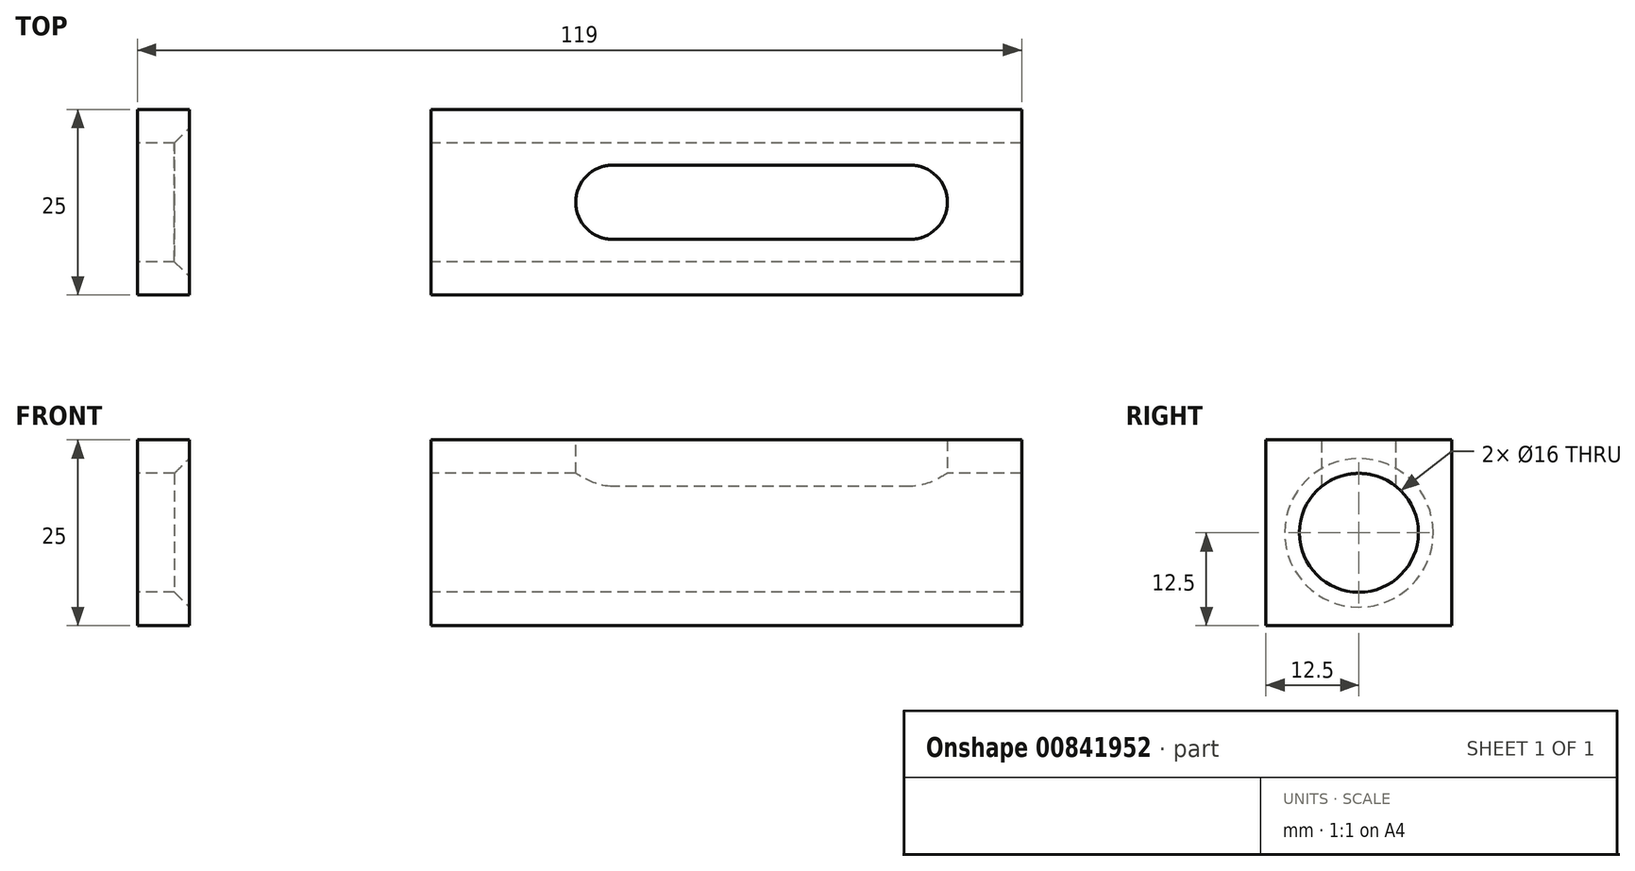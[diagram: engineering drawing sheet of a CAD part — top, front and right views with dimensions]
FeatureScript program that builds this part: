
annotation { "Feature Type Name" : "Feature", "Feature Type Description" : "" }
export const myFeature = defineFeature(function(context is Context, id is Id, definition is map)
    precondition{}
    {
        {
            var Q0;
            Q0=qCreatedBy(makeId("Top.planeOp"),FACE);
            var sketch = newSketch(context, id + "F0", { "sketchPlane" : qUnion([Q0])});
            skLineSegment(sketch, "E0.bottom", {"start": v(-59.5, 12.5) * mm, "end": v(59.5, 12.5) * mm});
            skLineSegment(sketch, "E0.top", {"start": v(-59.5, -12.5) * mm, "end": v(59.5, -12.5) * mm});
            skLineSegment(sketch, "E0.left", {"start": v(-59.5, 12.5) * mm, "end": v(-59.5, -12.5) * mm});
            skLineSegment(sketch, "E0.right", {"start": v(59.5, 12.5) * mm, "end": v(59.5, -12.5) * mm});
            skPoint(sketch, "E0.middle", {"position": v(0, 0) * mm});
            skSolve(sketch);
        }
        {
            var Q0;
            Q0 = qSketchRegion(id + "F0", true);
            extrude(context, id + "F1", {"entities" : qUnion([Q0]), "depth" : 25 * mm, "offsetDistance" : 25 * mm});
        }
        {
            var Q0;
            Q0=makeQuery(id+"F1.opExtrude","SWEPT_FACE",FACE,{"disambiguationData":[OSD([sQuery(id+"F0.wireOp",EDGE,"E0.left")])]});
            var sketch = newSketch(context, id + "F2", { "sketchPlane" : qUnion([Q0])});
            skLineSegment(sketch, "E1", {"start": v(0, 25) * mm, "end": v(0, 0) * mm});
            skCircle(sketch, "E2", {"center": v(0, 12.5) * mm, "radius": 8 * mm});
            skSolve(sketch);
        }
        {
            var Q0;
            {var subQ0=sQuery(id+"F2.wireOp",EDGE,"E2");var subQ1=sQuery(id+"F2.wireOp",EDGE,"E1");var subQ2=makeQuery(id+"F2.imprint","INTERSECT",VERTEX,{"disambiguationData":[OD(0.0)],"derivedFrom":[subQ1,subQ0]});Q0=makeQuery(id+"F2.imprint","IMPRINT",FACE,{"disambiguationData":[TD([[makeQuery(id+"F2.imprint","IMPRINT",EDGE,{"disambiguationData":[TD([[subQ2,-1.0]])],"derivedFrom":subQ1}),1.0]])]});}
            var Q1;
            {var subQ0=sQuery(id+"F2.wireOp",EDGE,"E2");var subQ1=sQuery(id+"F2.wireOp",EDGE,"E1");var subQ2=makeQuery(id+"F2.imprint","INTERSECT",VERTEX,{"disambiguationData":[OD(0.0)],"derivedFrom":[subQ1,subQ0]});Q1=makeQuery(id+"F2.imprint","IMPRINT",FACE,{"disambiguationData":[TD([[makeQuery(id+"F2.imprint","IMPRINT",EDGE,{"disambiguationData":[TD([[subQ2,-1.0]])],"derivedFrom":subQ1}),-1.0]])]});}
            extrude(context, id + "F3", {"entities" : qUnion([Q0, Q1]), "operationType" : NewBodyOperationType.REMOVE, "endBound" : BoundingType.THROUGH_ALL, "oppositeDirection" : true, "depth" : 25 * mm, "offsetDistance" : 25 * mm});
        }
        {
            var Q0;
            Q0=makeQuery(id+"F1.opExtrude","CAP_FACE",FACE,{"disambiguationData":[OSD([sQuery(id+"F0.wireOp",EDGE,"E0.bottom"),sQuery(id+"F0.wireOp",EDGE,"E0.top"),sQuery(id+"F0.wireOp",EDGE,"E0.left"),sQuery(id+"F0.wireOp",EDGE,"E0.right")])],"isStart":false});
            var sketch = newSketch(context, id + "F4", { "sketchPlane" : qUnion([Q0])});
            skLineSegment(sketch, "E3.bottom", {"start": v(-52.5, 12.5) * mm, "end": v(-20, 12.5) * mm});
            skLineSegment(sketch, "E3.top", {"start": v(-52.5, -12.5) * mm, "end": v(-20, -12.5) * mm});
            skLineSegment(sketch, "E3.left", {"start": v(-52.5, 12.5) * mm, "end": v(-52.5, -12.5) * mm});
            skLineSegment(sketch, "E3.right", {"start": v(-20, 12.5) * mm, "end": v(-20, -12.5) * mm});
            skSolve(sketch);
        }
        {
            var Q0;
            Q0 = qSketchRegion(id + "F4", true);
            extrude(context, id + "F5", {"entities" : qUnion([Q0]), "operationType" : NewBodyOperationType.REMOVE, "endBound" : BoundingType.THROUGH_ALL, "oppositeDirection" : true, "depth" : 25 * mm, "offsetDistance" : 25 * mm});
        }
        {
            var Q0;
            Q0=makeQuery(id+"F5.boolean.opBoolean","INTERSECT",EDGE,{"derivedFrom":[makeQuery(id+"F3.boolean.opBoolean","COPY",FACE,{"derivedFrom":makeQuery(id+"F3.opExtrude","SWEPT_FACE",FACE,{"disambiguationData":[OSD([sQuery(id+"F2.wireOp",EDGE,"E2")])]})}),makeQuery(id+"F5.opExtrude","SWEPT_FACE",FACE,{"disambiguationData":[OSD([sQuery(id+"F4.wireOp",EDGE,"E3.left")])]})]});
            chamfer(context, id + "F6", {"entities" : qUnion([Q0]), "width" : 2 * mm, "tangentPropagation" : true});
        }
        {
            var Q0;
            {var subQ0=sQuery(id+"F0.wireOp",EDGE,"E0.bottom");var subQ1=sQuery(id+"F0.wireOp",EDGE,"E0.right");var subQ2=sQuery(id+"F0.wireOp",EDGE,"E0.top");Q0=makeQuery(id+"F5.boolean.opBoolean","SPLIT",FACE,{"disambiguationData":[TD([makeQuery(id+"F1.opExtrude","SWEPT_FACE",FACE,{"disambiguationData":[OSD([subQ1])]})])],"derivedFrom":makeQuery(id+"F1.opExtrude","CAP_FACE",FACE,{"disambiguationData":[OSD([subQ0,subQ2,sQuery(id+"F0.wireOp",EDGE,"E0.left"),subQ1])],"isStart":false})});}
            var sketch = newSketch(context, id + "F7", { "sketchPlane" : qUnion([Q0])});
            skLineSegment(sketch, "E4.bottom", {"start": v(-0.5, 5) * mm, "end": v(49.5, 5) * mm});
            skLineSegment(sketch, "E4.top", {"start": v(-0.5, -5) * mm, "end": v(49.5, -5) * mm});
            skLineSegment(sketch, "E4.left", {"start": v(-0.5, 5) * mm, "end": v(-0.5, -5) * mm});
            skLineSegment(sketch, "E4.right", {"start": v(49.5, 5) * mm, "end": v(49.5, -5) * mm});
            skPoint(sketch, "E4.middle", {"position": v(24.5, 0) * mm});
            skLineSegment(sketch, "E5", {"start": v(-20, 0) * mm, "end": v(59.5, 0) * mm});
            skSolve(sketch);
        }
        {
            var Q0;
            Q0 = qSketchRegion(id + "F7", true);
            extrude(context, id + "F8", {"entities" : qUnion([Q0]), "operationType" : NewBodyOperationType.REMOVE, "oppositeDirection" : true, "depth" : 10 * mm, "offsetDistance" : 25 * mm});
        }
        {
            var Q0;
            Q0=makeQuery(id+"F8.boolean.opBoolean","COPY",EDGE,{"derivedFrom":makeQuery(id+"F8.opExtrude","SWEPT_EDGE",EDGE,{"disambiguationData":[OSD([sQuery(id+"F7.wireOp",EDGE,"E4.bottom"),sQuery(id+"F7.wireOp",EDGE,"E4.left")])]})});
            var Q1;
            Q1=makeQuery(id+"F8.boolean.opBoolean","COPY",EDGE,{"derivedFrom":makeQuery(id+"F8.opExtrude","SWEPT_EDGE",EDGE,{"disambiguationData":[OSD([sQuery(id+"F7.wireOp",EDGE,"E4.top"),sQuery(id+"F7.wireOp",EDGE,"E4.left")])]})});
            fillet(context, id + "F9", {"entities" : qUnion([Q0, Q1]), "radius" : 5 * mm, "tangentPropagation" : true, "allowEdgeOverflow" : false});
        }
        {
            var Q0;
            Q0=makeQuery(id+"F8.boolean.opBoolean","COPY",EDGE,{"derivedFrom":makeQuery(id+"F8.opExtrude","SWEPT_EDGE",EDGE,{"disambiguationData":[OSD([sQuery(id+"F7.wireOp",EDGE,"E4.bottom"),sQuery(id+"F7.wireOp",EDGE,"E4.right")])]})});
            var Q1;
            Q1=makeQuery(id+"F8.boolean.opBoolean","COPY",EDGE,{"derivedFrom":makeQuery(id+"F8.opExtrude","SWEPT_EDGE",EDGE,{"disambiguationData":[OSD([sQuery(id+"F7.wireOp",EDGE,"E4.top"),sQuery(id+"F7.wireOp",EDGE,"E4.right")])]})});
            fillet(context, id + "F10", {"entities" : qUnion([Q0, Q1]), "radius" : 5 * mm, "tangentPropagation" : true, "allowEdgeOverflow" : false});
        }
    });
